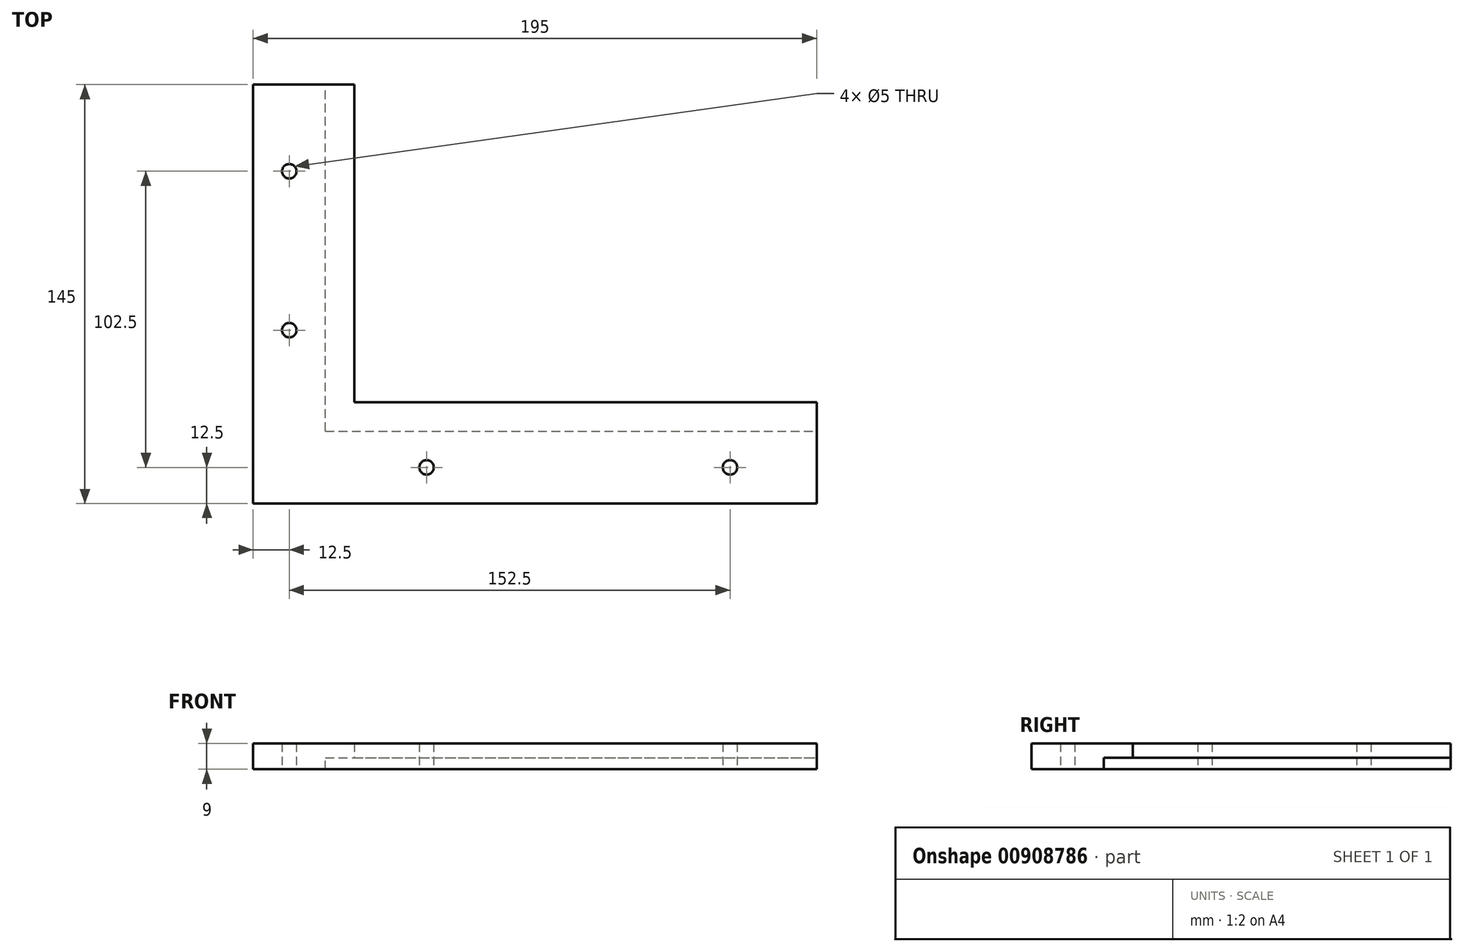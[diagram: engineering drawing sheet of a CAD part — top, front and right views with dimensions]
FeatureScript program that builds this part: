
annotation { "Feature Type Name" : "Feature", "Feature Type Description" : "" }
export const myFeature = defineFeature(function(context is Context, id is Id, definition is map)
    precondition{}
    {
        {
            var Q0;
            Q0=qCreatedBy(makeId("Top.planeOp"),FACE);
            var sketch = newSketch(context, id + "F0", { "sketchPlane" : qUnion([Q0])});
            skEllipticalArc(sketch, "E0", {});
            skLineSegment(sketch, "E1", {"start": v(-176, 0) * mm, "end": v(-176, -130) * mm});
            skPoint(sketch, "E1.endSnap0", {"position": v(0, -130) * mm});
            skLineSegment(sketch, "E2", {"start": v(-176, -130) * mm, "end": v(0, -130) * mm});
            skLineSegment(sketch, "E3", {"start": v(-176, 0) * mm, "end": v(-200, 0) * mm});
            skLineSegment(sketch, "E4", {"start": v(-200, 0) * mm, "end": v(-200, -150) * mm});
            skLineSegment(sketch, "E5", {"start": v(-200, -150) * mm, "end": v(0, -150) * mm});
            skLineSegment(sketch, "E6", {"start": v(0, -150) * mm, "end": v(0, -130) * mm});
            const initialGuessF0  = {"E0": [0, 0, 1, 0, 0.176, 0.13, 3.141592653589793, 4.71238898038469]};
            skSetInitialGuess(sketch, initialGuessF0);
            skSolve(sketch);
        }
        {
            var Q0;
            Q0=qSketchRegion(id+"F0",true);
            extrude(context, id + "F1", {"entities" : qUnion([Q0]), "depth" : 12 * mm, "offsetDistance" : 25 * mm});
        }
        {
            var Q0;
            Q0=makeQuery(id+"F1.opExtrude","SWEPT_FACE",FACE,{"disambiguationData":[OSD([sQuery(id+"F0.wireOp",EDGE,"E5")])]});
            var sketch = newSketch(context, id + "F2", { "sketchPlane" : qUnion([Q0])});
            skLineSegment(sketch, "E7.bottom", {"start": v(-200, 16) * mm, "end": v(0, 16) * mm});
            skLineSegment(sketch, "E7.top", {"start": v(-200, -4) * mm, "end": v(0, -4) * mm});
            skLineSegment(sketch, "E7.left", {"start": v(-200, 16) * mm, "end": v(-200, -4) * mm});
            skLineSegment(sketch, "E7.right", {"start": v(0, 16) * mm, "end": v(0, -4) * mm});
            skSolve(sketch);
        }
        {
            var Q0;
            Q0=qSketchRegion(id+"F2",true);
            extrude(context, id + "F3", {"entities" : qUnion([Q0]), "operationType" : NewBodyOperationType.ADD, "depth" : 5 * mm, "offsetDistance" : 25 * mm});
        }
        {
            var Q0;
            Q0=makeQuery(id+"F3.boolean.opBoolean","MERGE",FACE,{"derivedFrom":[makeQuery(id+"F1.opExtrude","SWEPT_FACE",FACE,{"disambiguationData":[OSD([sQuery(id+"F0.wireOp",EDGE,"E4")])]}),makeQuery(id+"F3.opExtrude","SWEPT_FACE",FACE,{"disambiguationData":[OSD([sQuery(id+"F2.wireOp",EDGE,"E7.left")])]})]});
            var sketch = newSketch(context, id + "F4", { "sketchPlane" : qUnion([Q0])});
            skLineSegment(sketch, "E8.bottom", {"start": v(155, 16) * mm, "end": v(0, 16) * mm});
            skLineSegment(sketch, "E8.top", {"start": v(155, -4) * mm, "end": v(0, -4) * mm});
            skLineSegment(sketch, "E8.left", {"start": v(155, 16) * mm, "end": v(155, -4) * mm});
            skLineSegment(sketch, "E8.right", {"start": v(0, 16) * mm, "end": v(0, -4) * mm});
            skSolve(sketch);
        }
        {
            var Q0;
            Q0=qSketchRegion(id+"F4",true);
            extrude(context, id + "F5", {"entities" : qUnion([Q0]), "operationType" : NewBodyOperationType.ADD, "depth" : 5 * mm, "offsetDistance" : 25 * mm});
        }
        {
            var Q0;
            Q0=makeQuery(id+"F5.boolean.opBoolean","MERGE",FACE,{"derivedFrom":[makeQuery(id+"F3.opExtrude","SWEPT_FACE",FACE,{"disambiguationData":[OSD([sQuery(id+"F2.wireOp",EDGE,"E7.top")])]}),makeQuery(id+"F5.opExtrude","SWEPT_FACE",FACE,{"disambiguationData":[OSD([sQuery(id+"F4.wireOp",EDGE,"E8.top")])]})]});
            var sketch = newSketch(context, id + "F6", { "sketchPlane" : qUnion([Q0])});
            skLineSegment(sketch, "E9", {"start": v(0, 175) * mm, "end": v(-225, 175) * mm});
            skLineSegment(sketch, "E10", {"start": v(-225, 175) * mm, "end": v(-225, 0) * mm});
            skLineSegment(sketch, "E11", {"start": v(-225, 0) * mm, "end": v(-205, 0) * mm});
            skLineSegment(sketch, "E12", {"start": v(-205, 0) * mm, "end": v(-205, 155) * mm});
            skLineSegment(sketch, "E13", {"start": v(-205, 155) * mm, "end": v(0, 155) * mm});
            skLineSegment(sketch, "E14", {"start": v(0, 155) * mm, "end": v(0, 175) * mm});
            skCircle(sketch, "E15", {"center": v(-212.5, 60) * mm, "radius": 2.5 * mm});
            skCircle(sketch, "E16", {"center": v(-212.5, 115) * mm, "radius": 2.5 * mm});
            skCircle(sketch, "E17", {"center": v(-165, 162.5) * mm, "radius": 2.5 * mm});
            skCircle(sketch, "E18", {"center": v(-60, 162.5) * mm, "radius": 2.5 * mm});
            skSolve(sketch);
        }
        {
            var Q0;
            Q0=qSketchRegion(id+"F6",true);
            extrude(context, id + "F7", {"entities" : qUnion([Q0]), "operationType" : NewBodyOperationType.ADD, "oppositeDirection" : true, "depth" : 25 * mm, "offsetDistance" : 25 * mm});
        }
        {
            var Q0;
            Q0=makeQuery(id+"F5.boolean.opBoolean","MERGE",FACE,{"derivedFrom":[makeQuery(id+"F3.opExtrude","SWEPT_FACE",FACE,{"disambiguationData":[OSD([sQuery(id+"F2.wireOp",EDGE,"E7.bottom")])]}),makeQuery(id+"F5.opExtrude","SWEPT_FACE",FACE,{"disambiguationData":[OSD([sQuery(id+"F4.wireOp",EDGE,"E8.bottom")])]})]});
            var sketch = newSketch(context, id + "F8", { "sketchPlane" : qUnion([Q0])});
            skLineSegment(sketch, "E19", {"start": v(-205, 0) * mm, "end": v(-190, 0) * mm});
            skLineSegment(sketch, "E20", {"start": v(-190, 0) * mm, "end": v(-190, -140) * mm});
            skLineSegment(sketch, "E21", {"start": v(-190, -140) * mm, "end": v(0, -140) * mm});
            skLineSegment(sketch, "E22", {"start": v(0, -140) * mm, "end": v(0, -155) * mm});
            skLineSegment(sketch, "E23", {"start": v(0, -155) * mm, "end": v(-205, -155) * mm});
            skLineSegment(sketch, "E24", {"start": v(-205, -155) * mm, "end": v(-205, 0) * mm});
            skSolve(sketch);
        }
        {
            var Q0;
            Q0=qSketchRegion(id+"F8",true);
            extrude(context, id + "F9", {"entities" : qUnion([Q0]), "operationType" : NewBodyOperationType.ADD, "depth" : 5 * mm, "offsetDistance" : 25 * mm});
        }
        {
            var Q0;
            Q0=qCreatedBy(makeId("Top.planeOp"),FACE);
            var sketch = newSketch(context, id + "F10", { "sketchPlane" : qUnion([Q0])});
            skLineSegment(sketch, "E25.bottom", {"start": v(-225, 0) * mm, "end": v(0, 0) * mm});
            skLineSegment(sketch, "E25.top", {"start": v(-225, -30) * mm, "end": v(0, -30) * mm});
            skLineSegment(sketch, "E25.left", {"start": v(-225, 0) * mm, "end": v(-225, -30) * mm});
            skLineSegment(sketch, "E25.right", {"start": v(0, 0) * mm, "end": v(0, -30) * mm});
            skLineSegment(sketch, "E26.bottom", {"start": v(0, -175) * mm, "end": v(-30, -175) * mm});
            skLineSegment(sketch, "E26.top", {"start": v(0, 0) * mm, "end": v(-30, 0) * mm});
            skLineSegment(sketch, "E26.left", {"start": v(0, -175) * mm, "end": v(0, 0) * mm});
            skLineSegment(sketch, "E26.right", {"start": v(-30, -175) * mm, "end": v(-30, 0) * mm});
            skSolve(sketch);
        }
        {
            var Q0;
            Q0=qSketchRegion(id+"F10",true);
            extrude(context, id + "F11", {"entities" : qUnion([Q0]), "operationType" : NewBodyOperationType.REMOVE, "endBound" : BoundingType.SYMMETRIC, "oppositeDirection" : true, "depth" : 50 * mm, "offsetDistance" : 25 * mm});
        }
        {
            var Q0;
            Q0=makeQuery(id+"F11.boolean.opBoolean","COPY",FACE,{"derivedFrom":makeQuery(id+"F11.opExtrude","SWEPT_FACE",FACE,{"disambiguationData":[OSD([sQuery(id+"F10.wireOp",EDGE,"E26.right")])]})});
            var sketch = newSketch(context, id + "F12", { "sketchPlane" : qUnion([Q0])});
            skLineSegment(sketch, "E27.bottom", {"start": v(-175, -4) * mm, "end": v(-30, -4) * mm});
            skLineSegment(sketch, "E27.top", {"start": v(-175, 12) * mm, "end": v(-30, 12) * mm});
            skLineSegment(sketch, "E27.left", {"start": v(-175, -4) * mm, "end": v(-175, 12) * mm});
            skLineSegment(sketch, "E27.right", {"start": v(-30, -4) * mm, "end": v(-30, 12) * mm});
            skSolve(sketch);
        }
        {
            var Q0;
            Q0 = qSketchRegion(id + "F12", true);
            extrude(context, id + "F13", {"entities" : qUnion([Q0]), "operationType" : NewBodyOperationType.REMOVE, "endBound" : BoundingType.THROUGH_ALL, "oppositeDirection" : true, "depth" : 25 * mm, "offsetDistance" : 25 * mm});
        }
    });
